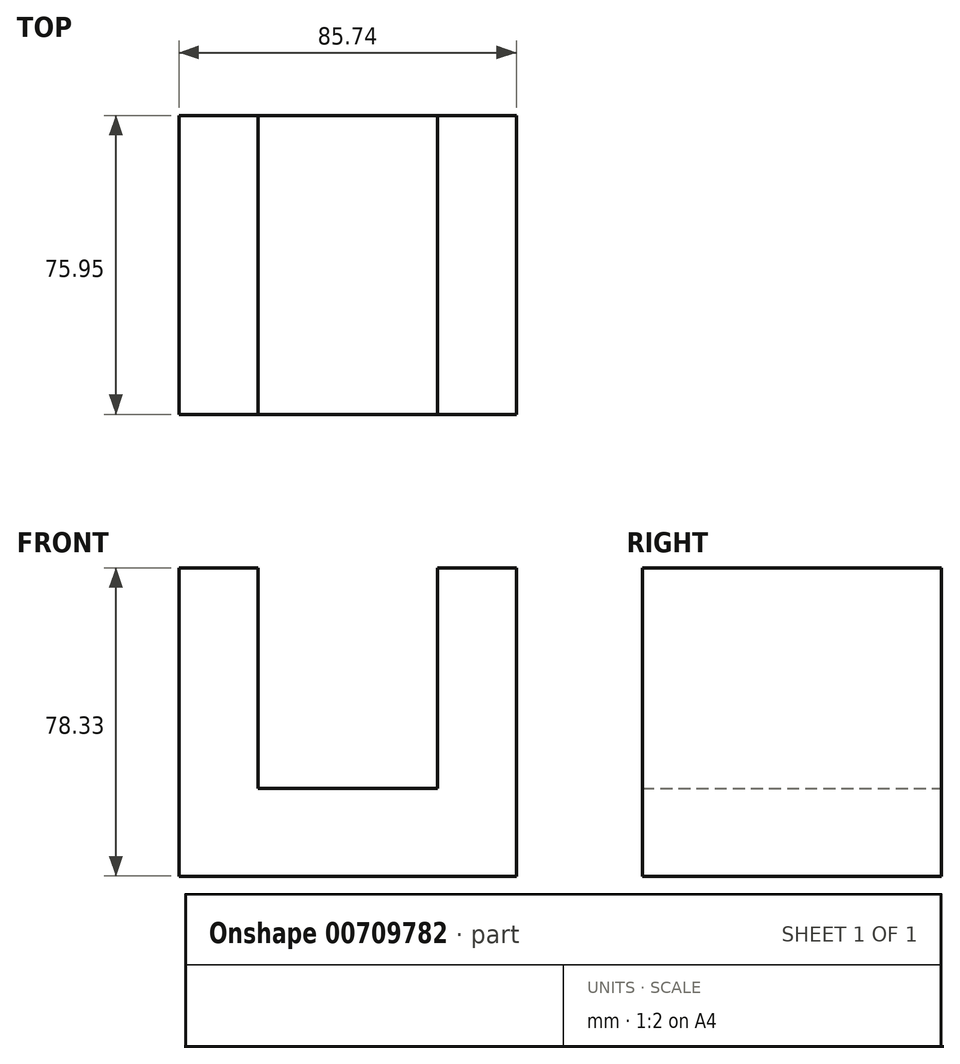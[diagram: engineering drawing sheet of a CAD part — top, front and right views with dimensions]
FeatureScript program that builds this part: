
annotation { "Feature Type Name" : "Feature", "Feature Type Description" : "" }
export const myFeature = defineFeature(function(context is Context, id is Id, definition is map)
    precondition{}
    {
        {
            var Q0;
            Q0=qCreatedBy(makeId("Front.planeOp"),FACE);
            var sketch = newSketch(context, id + "F0", { "sketchPlane" : qUnion([Q0])});
            skLineSegment(sketch, "E0.bottom", {"start": v(0, 0) * mm, "end": v(42.87, 0) * mm});
            skLineSegment(sketch, "E0.top", {"start": v(0, -22.31) * mm, "end": v(42.87, -22.31) * mm});
            skLineSegment(sketch, "E0.left", {"start": v(0, 0) * mm, "end": v(0, -22.31) * mm});
            skLineSegment(sketch, "E0.right", {"start": v(42.87, 0) * mm, "end": v(42.87, -22.31) * mm});
            skLineSegment(sketch, "E1.bottom", {"start": v(42.87, 0) * mm, "end": v(22.82, 0) * mm});
            skLineSegment(sketch, "E1.top", {"start": v(42.87, 56.02) * mm, "end": v(22.82, 56.02) * mm});
            skLineSegment(sketch, "E1.left", {"start": v(42.87, 0) * mm, "end": v(42.87, 56.02) * mm});
            skLineSegment(sketch, "E1.right", {"start": v(22.82, 0) * mm, "end": v(22.82, 56.02) * mm});
            skLineSegment(sketch, "E2.MirrorCS", {"start": v(-42.87, 0) * mm, "end": v(-22.82, 0) * mm});
            skLineSegment(sketch, "E3.MirrorCS", {"start": v(0, -22.31) * mm, "end": v(-42.87, -22.31) * mm});
            skLineSegment(sketch, "E4.MirrorCS", {"start": v(-42.87, 56.02) * mm, "end": v(-22.82, 56.02) * mm});
            skLineSegment(sketch, "E5.MirrorCS", {"start": v(-42.87, 0) * mm, "end": v(-42.87, -22.31) * mm});
            skLineSegment(sketch, "E6.MirrorCS", {"start": v(0, 0) * mm, "end": v(-42.87, 0) * mm});
            skLineSegment(sketch, "E7.MirrorCS", {"start": v(-22.82, 0) * mm, "end": v(-22.82, 56.02) * mm});
            skLineSegment(sketch, "E8.MirrorCS", {"start": v(-42.87, 0) * mm, "end": v(-42.87, 56.02) * mm});
            skSolve(sketch);
        }
        {
            var Q0;
            Q0 = qSketchRegion(id + "F0", true);
            extrude(context, id + "F1", {"entities" : qUnion([Q0]), "depth" : 75.95 * mm, "offsetDistance" : 25.4 * mm});
        }
    });
